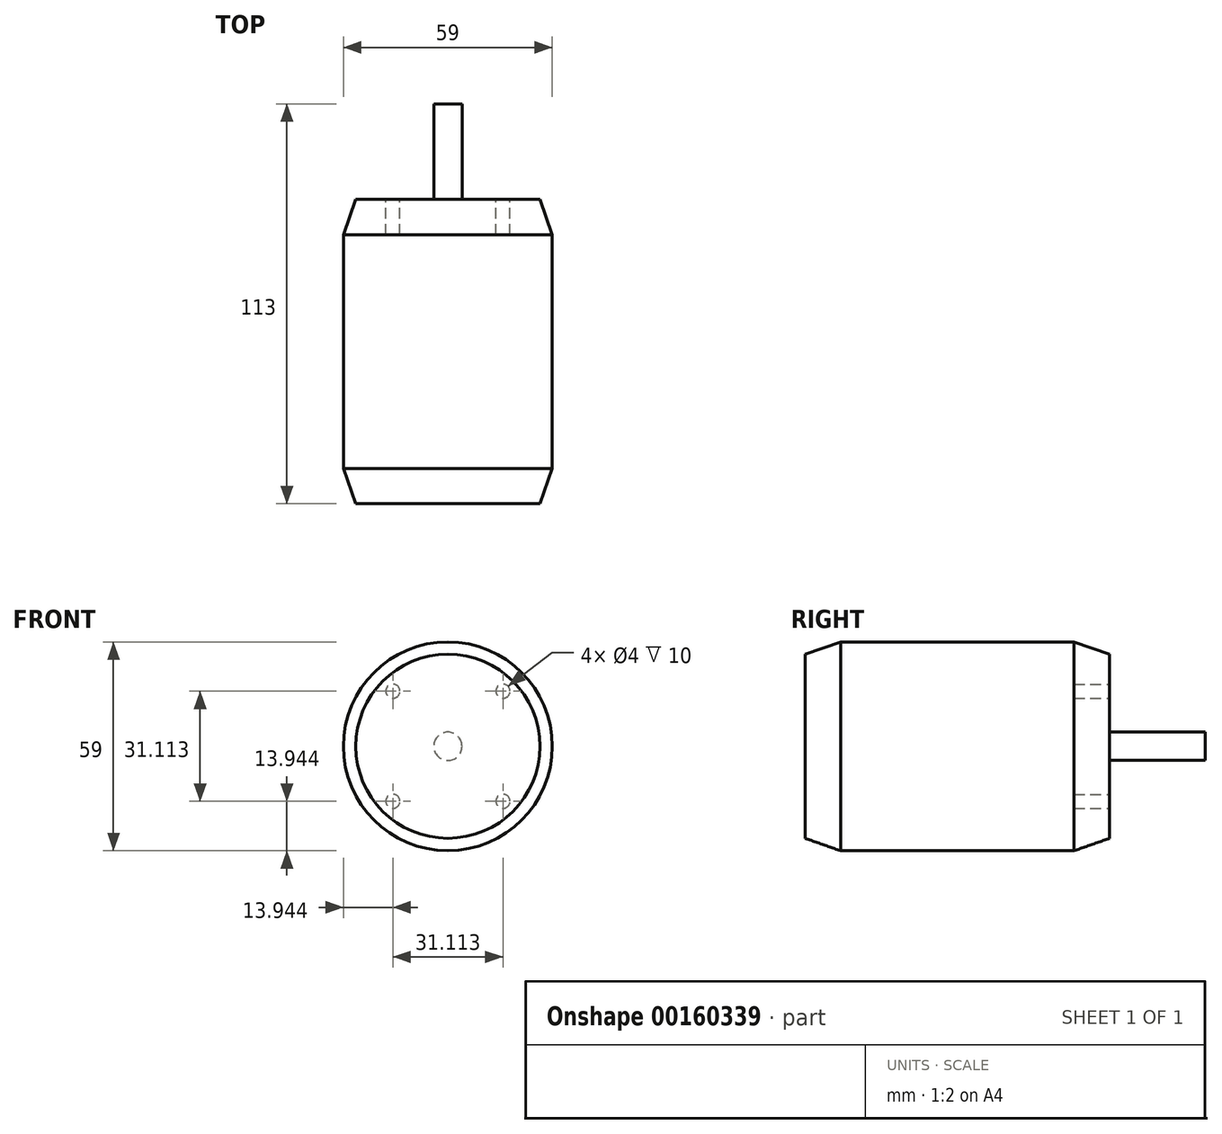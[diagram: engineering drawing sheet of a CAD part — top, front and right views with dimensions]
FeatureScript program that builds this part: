
annotation { "Feature Type Name" : "Feature", "Feature Type Description" : "" }
export const myFeature = defineFeature(function(context is Context, id is Id, definition is map)
    precondition{}
    {
        {
            var Q0;
            Q0=qCreatedBy(makeId("Front.planeOp"),FACE);
            var sketch = newSketch(context, id + "F0", { "sketchPlane" : qUnion([Q0])});
            skCircle(sketch, "E0", {"center": v(0, 0) * mm, "radius": 29.5 * mm});
            skCircle(sketch, "E1", {"center": v(0, 0) * mm, "radius": 4 * mm});
            skCircle(sketch, "E2", {"center": v(0, 0) * mm, "radius": 22 * mm, "construction": true});
            skLineSegment(sketch, "E3", {"start": v(0, 0) * mm, "end": v(-15.56, 15.56) * mm, "construction": true});
            skCircle(sketch, "E4", {"center": v(-15.56, 15.56) * mm, "radius": 2 * mm});
            skCircle(sketch, "E5.1.0", {"center": v(-15.56, -15.56) * mm, "radius": 2 * mm});
            skCircle(sketch, "E5.2.0", {"center": v(15.56, -15.56) * mm, "radius": 2 * mm});
            skCircle(sketch, "E6.1.3.0", {"center": v(15.56, 15.56) * mm, "radius": 2 * mm});
            skSolve(sketch);
        }
        {
            var Q0;
            Q0=makeQuery(id+"F0.imprint","IMPRINT",FACE,{"disambiguationData":[TD([[makeQuery(id+"F0.imprint","IMPRINT",EDGE,{"derivedFrom":sQuery(id+"F0.wireOp",EDGE,"E0")}),1.0]])]});
            var Q1;
            Q1=makeQuery(id+"F0.imprint","IMPRINT",FACE,{"disambiguationData":[TD([[makeQuery(id+"F0.imprint","IMPRINT",EDGE,{"derivedFrom":sQuery(id+"F0.wireOp",EDGE,"E1")}),1.0]])]});
            var Q2;
            Q2=makeQuery(id+"F0.imprint","IMPRINT",FACE,{"disambiguationData":[TD([[makeQuery(id+"F0.imprint","IMPRINT",EDGE,{"derivedFrom":sQuery(id+"F0.wireOp",EDGE,"E6.1.3.0")}),1.0]])]});
            var Q3;
            Q3=makeQuery(id+"F0.imprint","IMPRINT",FACE,{"disambiguationData":[TD([[makeQuery(id+"F0.imprint","IMPRINT",EDGE,{"derivedFrom":sQuery(id+"F0.wireOp",EDGE,"E4")}),1.0]])]});
            var Q4;
            Q4=makeQuery(id+"F0.imprint","IMPRINT",FACE,{"disambiguationData":[TD([[makeQuery(id+"F0.imprint","IMPRINT",EDGE,{"derivedFrom":sQuery(id+"F0.wireOp",EDGE,"E5.1.0")}),1.0]])]});
            var Q5;
            Q5=makeQuery(id+"F0.imprint","IMPRINT",FACE,{"disambiguationData":[TD([[makeQuery(id+"F0.imprint","IMPRINT",EDGE,{"derivedFrom":sQuery(id+"F0.wireOp",EDGE,"E5.2.0")}),1.0]])]});
            extrude(context, id + "F1", {"entities" : qUnion([Q0, Q1, Q2, Q3, Q4, Q5]), "depth" : 86 * mm});
        }
        {
            var Q0;
            Q0=makeQuery(id+"F0.imprint","IMPRINT",FACE,{"disambiguationData":[TD([[makeQuery(id+"F0.imprint","IMPRINT",EDGE,{"derivedFrom":sQuery(id+"F0.wireOp",EDGE,"E1")}),1.0]])]});
            extrude(context, id + "F2", {"entities" : qUnion([Q0]), "operationType" : NewBodyOperationType.ADD, "oppositeDirection" : true, "depth" : 27 * mm});
        }
        {
            var Q0;
            Q0=makeQuery(id+"F0.imprint","IMPRINT",FACE,{"disambiguationData":[TD([[makeQuery(id+"F0.imprint","IMPRINT",EDGE,{"derivedFrom":sQuery(id+"F0.wireOp",EDGE,"E6.1.3.0")}),1.0]])]});
            var Q1;
            Q1=makeQuery(id+"F0.imprint","IMPRINT",FACE,{"disambiguationData":[TD([[makeQuery(id+"F0.imprint","IMPRINT",EDGE,{"derivedFrom":sQuery(id+"F0.wireOp",EDGE,"E4")}),1.0]])]});
            var Q2;
            Q2=makeQuery(id+"F0.imprint","IMPRINT",FACE,{"disambiguationData":[TD([[makeQuery(id+"F0.imprint","IMPRINT",EDGE,{"derivedFrom":sQuery(id+"F0.wireOp",EDGE,"E5.2.0")}),1.0]])]});
            var Q3;
            Q3=makeQuery(id+"F0.imprint","IMPRINT",FACE,{"disambiguationData":[TD([[makeQuery(id+"F0.imprint","IMPRINT",EDGE,{"derivedFrom":sQuery(id+"F0.wireOp",EDGE,"E5.1.0")}),1.0]])]});
            extrude(context, id + "F3", {"entities" : qUnion([Q0, Q1, Q2, Q3]), "operationType" : NewBodyOperationType.REMOVE, "depth" : 10 * mm});
        }
        {
            var Q0;
            Q0=makeQuery(id+"F1.opExtrude","CAP_EDGE",EDGE,{"disambiguationData":[OSD([sQuery(id+"F0.wireOp",EDGE,"E0")])],"isStart":true});
            chamfer(context, id + "F4", {"entities" : qUnion([Q0]), "chamferType" : ChamferType.TWO_OFFSETS, "width1" : 10 * mm, "oppositeDirection" : false, "width2" : 3.5 * mm, "tangentPropagation" : true});
        }
        {
            var Q0;
            Q0=makeQuery(id+"F1.opExtrude","CAP_EDGE",EDGE,{"disambiguationData":[OSD([sQuery(id+"F0.wireOp",EDGE,"E0")])],"isStart":false});
            chamfer(context, id + "F5", {"entities" : qUnion([Q0]), "chamferType" : ChamferType.TWO_OFFSETS, "width1" : 3.5 * mm, "oppositeDirection" : false, "width2" : 10 * mm, "tangentPropagation" : true});
        }
    });
